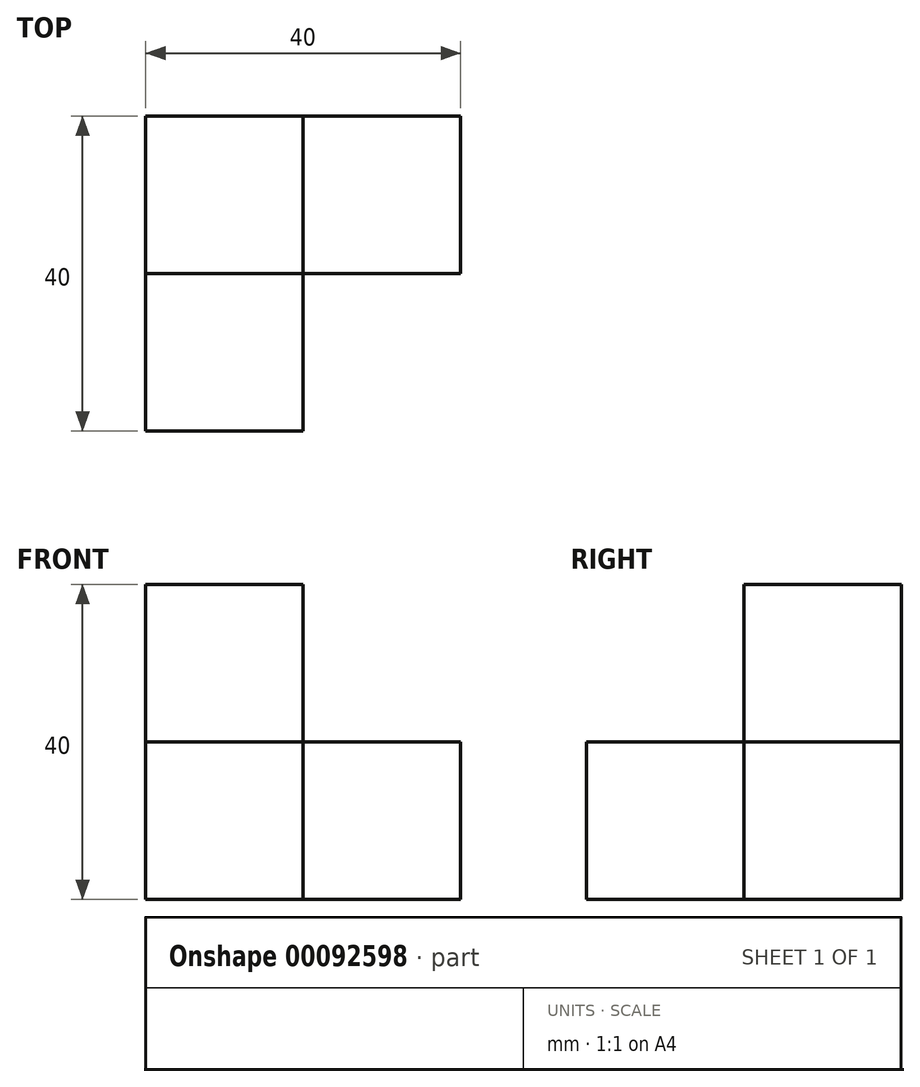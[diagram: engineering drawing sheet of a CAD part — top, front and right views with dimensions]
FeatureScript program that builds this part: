
annotation { "Feature Type Name" : "Feature", "Feature Type Description" : "" }
export const myFeature = defineFeature(function(context is Context, id is Id, definition is map)
    precondition{}
    {
        {
            var Q0;
            Q0=qCreatedBy(makeId("Top.planeOp"),FACE);
            var sketch = newSketch(context, id + "F0", { "sketchPlane" : qUnion([Q0])});
            skLineSegment(sketch, "E0.bottom", {"start": v(0, 0) * mm, "end": v(40, 0) * mm});
            skLineSegment(sketch, "E0.top", {"start": v(20, -20) * mm, "end": v(40, -20) * mm});
            skLineSegment(sketch, "E0.left", {"start": v(0, 0) * mm, "end": v(0, -20) * mm});
            skLineSegment(sketch, "E0.right", {"start": v(40, 0) * mm, "end": v(40, -20) * mm});
            skLineSegment(sketch, "E1.top", {"start": v(0, -40) * mm, "end": v(20, -40) * mm});
            skLineSegment(sketch, "E1.left", {"start": v(0, -20) * mm, "end": v(0, -40) * mm});
            skLineSegment(sketch, "E1.right", {"start": v(20, -20) * mm, "end": v(20, -40) * mm});
            skSolve(sketch);
        }
        {
            var Q0;
            Q0=makeQuery(id+"F0.imprint","IMPRINT",FACE,{"disambiguationData":[TD([[makeQuery(id+"F0.imprint","IMPRINT",EDGE,{"derivedFrom":sQuery(id+"F0.wireOp",EDGE,"E0.bottom")}),-1.0]])]});
            extrude(context, id + "F1", {"entities" : qUnion([Q0]), "depth" : 20 * mm});
        }
        {
            var Q0;
            Q0=makeQuery(id+"F1.opExtrude","CAP_FACE",FACE,{"disambiguationData":[OSD([sQuery(id+"F0.wireOp",EDGE,"E0.bottom"),sQuery(id+"F0.wireOp",EDGE,"E0.top"),sQuery(id+"F0.wireOp",EDGE,"E0.left"),sQuery(id+"F0.wireOp",EDGE,"E0.right"),sQuery(id+"F0.wireOp",EDGE,"E1.top"),sQuery(id+"F0.wireOp",EDGE,"E1.left"),sQuery(id+"F0.wireOp",EDGE,"E1.right")])],"isStart":false});
            var sketch = newSketch(context, id + "F2", { "sketchPlane" : qUnion([Q0])});
            skLineSegment(sketch, "E2.bottom", {"start": v(0, 0) * mm, "end": v(20, 0) * mm});
            skLineSegment(sketch, "E2.top", {"start": v(0, -20) * mm, "end": v(20, -20) * mm});
            skLineSegment(sketch, "E2.left", {"start": v(0, 0) * mm, "end": v(0, -20) * mm});
            skLineSegment(sketch, "E2.right", {"start": v(20, 0) * mm, "end": v(20, -20) * mm});
            skSolve(sketch);
        }
        {
            var Q0;
            Q0=makeQuery(id+"F2.imprint","IMPRINT",FACE,{"disambiguationData":[TD([[makeQuery(id+"F2.imprint","IMPRINT",EDGE,{"derivedFrom":sQuery(id+"F2.wireOp",EDGE,"E2.bottom")}),-1.0]])]});
            extrude(context, id + "F3", {"entities" : qUnion([Q0]), "operationType" : NewBodyOperationType.ADD, "depth" : 20 * mm});
        }
    });
